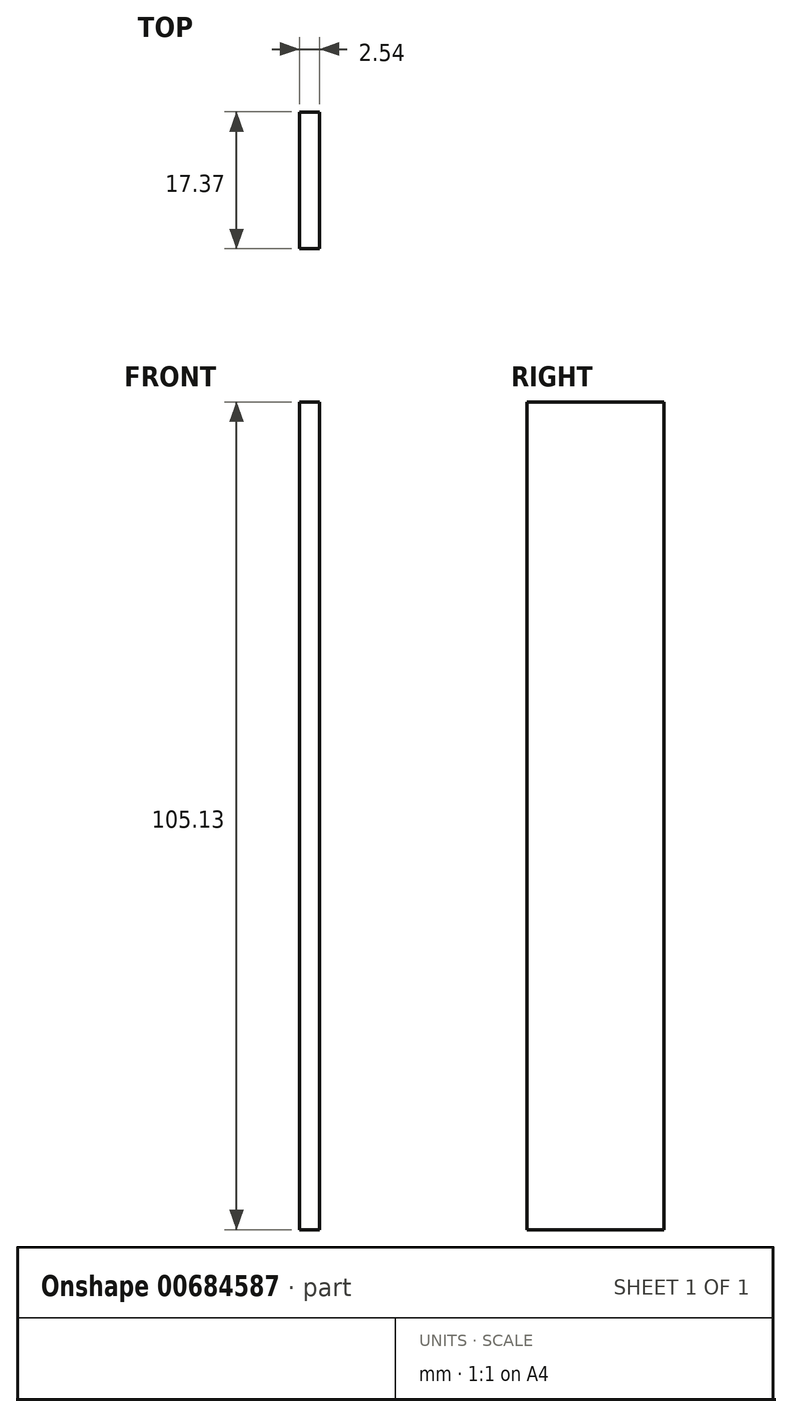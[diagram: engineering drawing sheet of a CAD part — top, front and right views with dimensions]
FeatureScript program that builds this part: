
annotation { "Feature Type Name" : "Feature", "Feature Type Description" : "" }
export const myFeature = defineFeature(function(context is Context, id is Id, definition is map)
    precondition{}
    {
        {
            var Q0;
            Q0=qCreatedBy(makeId("Right.planeOp"),FACE);
            var sketch = newSketch(context, id + "F0", { "sketchPlane" : qUnion([Q0])});
            skLineSegment(sketch, "E0.bottom", {"start": v(-8.84, 51.01) * mm, "end": v(8.53, 51.01) * mm});
            skLineSegment(sketch, "E0.top", {"start": v(-8.84, -54.12) * mm, "end": v(8.53, -54.12) * mm});
            skLineSegment(sketch, "E0.left", {"start": v(-8.84, 51.01) * mm, "end": v(-8.84, -54.12) * mm});
            skLineSegment(sketch, "E0.right", {"start": v(8.53, 51.01) * mm, "end": v(8.53, -54.12) * mm});
            skSolve(sketch);
        }
        {
            var Q0;
            Q0 = qSketchRegion(id + "F0", true);
            extrude(context, id + "F1", {"entities" : qUnion([Q0]), "depth" : 2.54 * mm, "offsetDistance" : 25.4 * mm});
        }
    });
